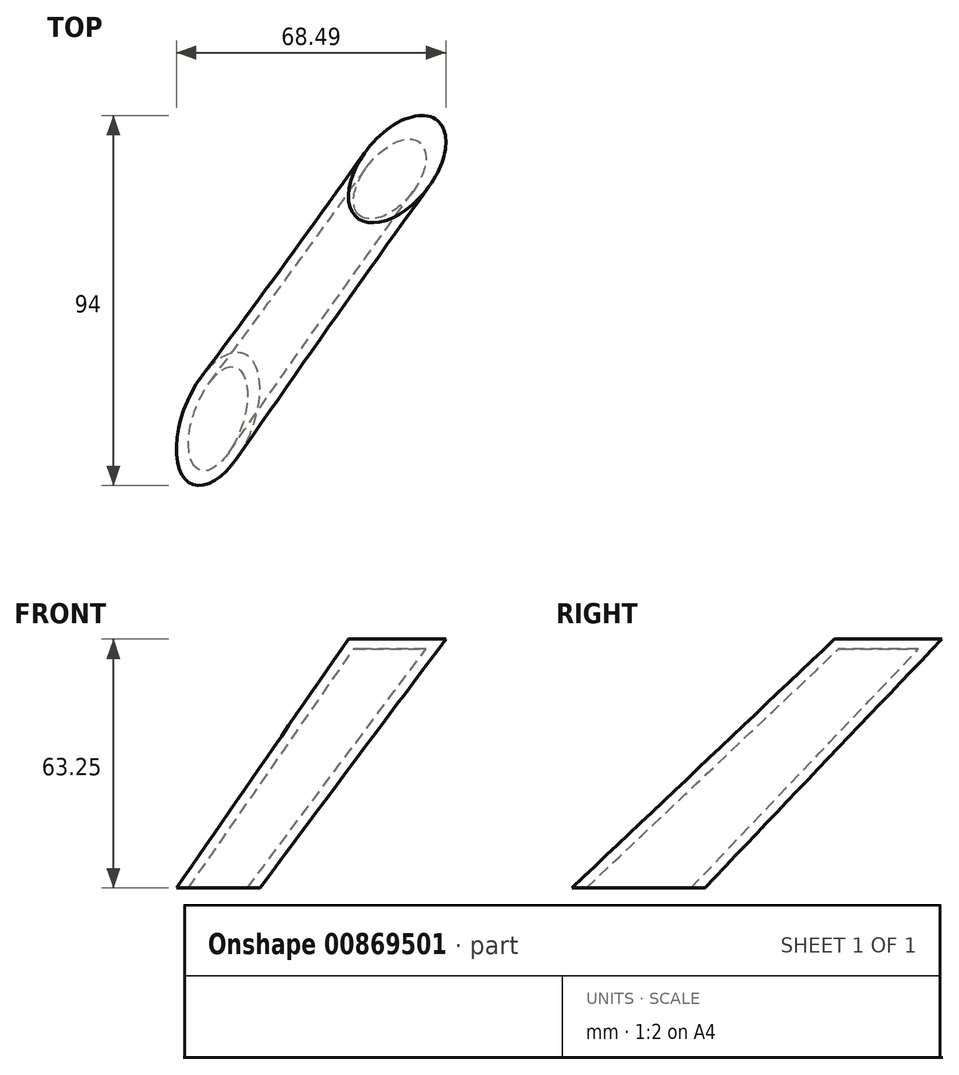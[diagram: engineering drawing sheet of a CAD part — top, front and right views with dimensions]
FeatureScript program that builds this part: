
annotation { "Feature Type Name" : "Feature", "Feature Type Description" : "" }
export const myFeature = defineFeature(function(context is Context, id is Id, definition is map)
    precondition{}
    {
        {
            var Q0;
            Q0=qCreatedBy(makeId("Top.planeOp"),FACE);
            var sketch = newSketch(context, id + "F0", { "sketchPlane" : qUnion([Q0])});
            skEllipse(sketch, "E0", {"center": v(-26.53, -22.2) * mm, "majorRadius": 23.1 * mm, "minorRadius": 13.42 * mm, "majorAxis": v(-0.34, -0.94)});
            skEllipse(sketch, "E1", {"center": v(-26.53, -22.2) * mm, "majorRadius": 17.82 * mm, "minorRadius": 8.97 * mm, "majorAxis": v(0.37, 0.93)});
            skSolve(sketch);
        }
        {
            var Q0;
            Q0=qCreatedBy(makeId("Top.planeOp"),FACE);
            cPlane(context, id + "F1", {"entities" : qUnion([Q0]), "cplaneType" : CPlaneType.OFFSET, "offset" : 63.25 * mm, "width" : 152.4 * mm, "height" : 152.4 * mm});
        }
        {
            var Q0;
            Q0=qCreatedBy(id+"F1.planeOp",FACE);
            var sketch = newSketch(context, id + "F2", { "sketchPlane" : qUnion([Q0])});
            skEllipse(sketch, "E2", {"center": v(18.96, 41.28) * mm, "majorRadius": 19.83 * mm, "minorRadius": 13.77 * mm, "majorAxis": v(0.63, 0.77)});
            skEllipse(sketch, "E3", {"center": v(18.96, 41.28) * mm, "majorRadius": 16.02 * mm, "minorRadius": 9.1 * mm, "majorAxis": v(0.64, 0.77)});
            skSolve(sketch);
        }
        {
            var Q0;
            Q0=makeQuery(id+"F2.imprint","IMPRINT",FACE,{"disambiguationData":[TD([[makeQuery(id+"F2.imprint","IMPRINT",EDGE,{"derivedFrom":sQuery(id+"F2.wireOp",EDGE,"E3")}),1.0]])]});
            var Q1;
            Q1=makeQuery(id+"F0.imprint","IMPRINT",FACE,{"disambiguationData":[TD([[makeQuery(id+"F0.imprint","IMPRINT",EDGE,{"derivedFrom":sQuery(id+"F0.wireOp",EDGE,"E1")}),1.0]])]});
            loft(context, id + "F3", {"sheetProfilesArray" : [{ "sheetProfileEntities" : qUnion([Q0]) }, { "sheetProfileEntities" : qUnion([Q1]) }]});
        }
        {
            var Q0;
            Q0=makeQuery(id+"F3.opLoft","CAP_FACE",FACE,{"disambiguationData":[OSD([makeQuery(id+"F0.imprint","IMPRINT",FACE,{"disambiguationData":[TD([[makeQuery(id+"F0.imprint","IMPRINT",EDGE,{"derivedFrom":sQuery(id+"F0.wireOp",EDGE,"E1")}),1.0]])]})])],"isStart":true});
            shell(context, id + "F4", {"entities" : qUnion([Q0]), "thickness" : 2.54 * mm});
        }
    });
